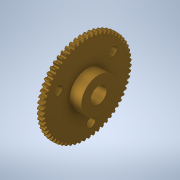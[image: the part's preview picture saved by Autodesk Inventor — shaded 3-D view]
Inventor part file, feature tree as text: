
AUTODESK INVENTOR PART (.ipt)
format: ipt  version: 2021 (Build 250183000, 183)  size: 619,008 bytes
history: native  units: mm
features: extrude x2, sketch x2, other x1, pattern_circular x1
ambient origin geometry x8: Origin, YZ Plane, XZ Plane, XY Plane, X Axis, Y Axis, Z Axis, Center Point
bodies: Body1 (feature_tree)
feature tree (6):
  other  "Sólido1"
  extrude  "Thread Entrance"  Depth=1.91mm
  pattern_circular  "Circular Pattern1"  Count=3  [1 undecoded]
  extrude  "Hole Machined"  Depth=10.0mm
  sketch  "Sketch3"  dims[d9=3.0mm d11=1.91mm]
  sketch  "Sketch4"  dims[d12=10.0mm d13=0.0mm d14=30.0mm d15=62.831853mm d17=5.5mm d18=10.0mm d19=0.0mm d20=10.833mm]
note: 1 required parameter value undecoded (feature->parameter linkage not recoverable at this tier; creation-order binding heuristic only, values carry confidence <= 0.55)
